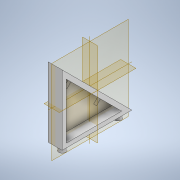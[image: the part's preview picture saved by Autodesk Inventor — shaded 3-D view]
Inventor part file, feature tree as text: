
AUTODESK INVENTOR PART (.ipt)
format: ipt  version: 2022.4 (Build 264492010, 492A)  size: 146,432 bytes
history: native  units: mm
features: extrude x4, sketch x4, mirror x1
ambient origin geometry x8: Origin, YZ Plane, XZ Plane, XY Plane, X Axis, Y Axis, Z Axis, Center Point
bodies: Solid1 (feature_tree)
feature tree (9):
  extrude  "Extrusion1"  Depth=50.0mm
  extrude  "Extrusion2"  Depth=3.0mm
  extrude  "Extrusion3"  Depth=5.0mm
  extrude  "Extrusion4"  Depth=10.0mm
  mirror  "Mirror1"
  sketch  "Sketch2"  dims[d0=50.0mm d1=50.0mm]
  sketch  "Sketch4"  dims[d2=10.0mm d3=0.0mm d8=3.0mm]
  sketch  "Sketch5"  dims[d9=7.0mm d10=0.0mm d11=5.0mm]
  sketch  "Sketch8"  dims[d12=5.0mm d13=20.0mm d15=40.0mm d16=10.0mm d18=10.0mm d20=5.0mm d21=0.0mm d31=70.710678mm d32=5.0mm d34=15.0mm d35=7.0mm d36=0.0mm]
